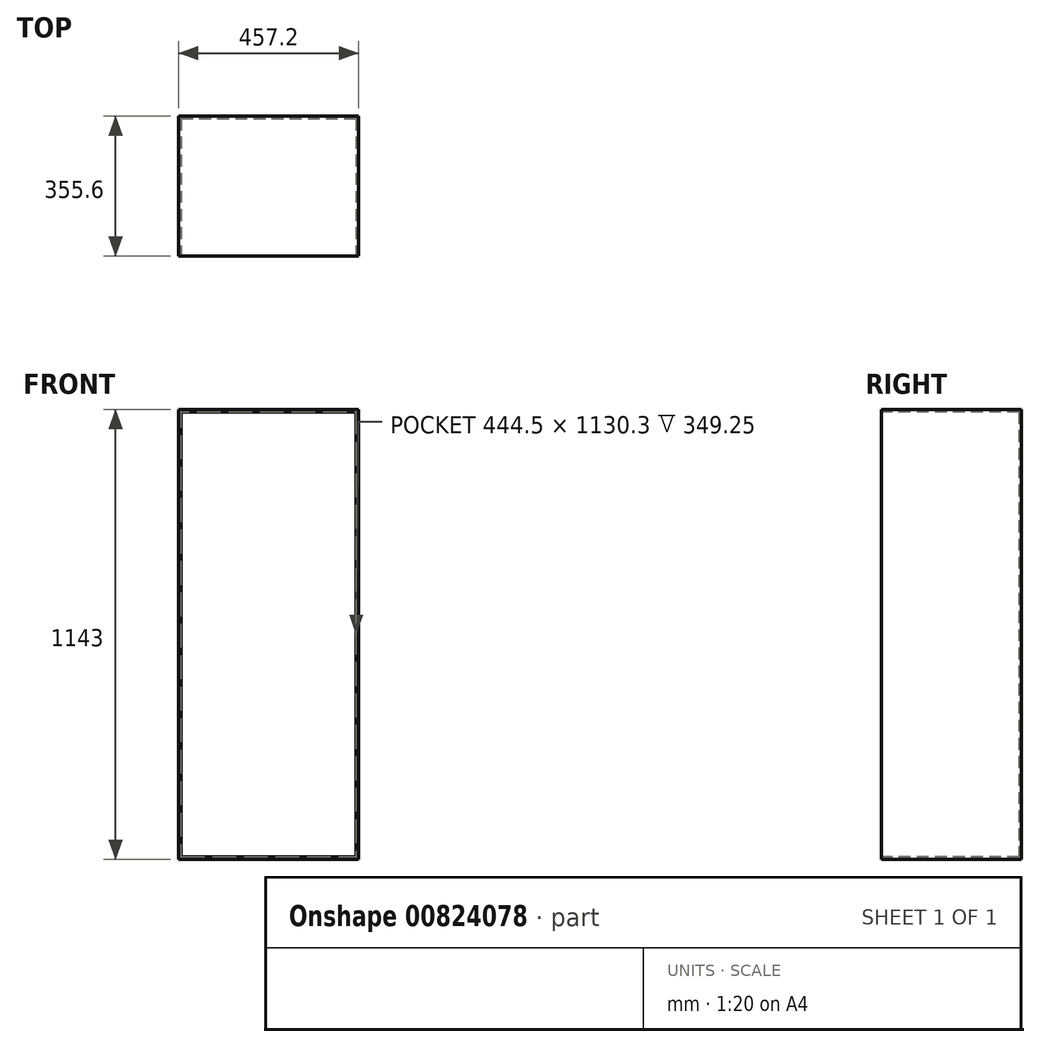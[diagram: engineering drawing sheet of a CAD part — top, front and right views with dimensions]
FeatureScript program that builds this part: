
annotation { "Feature Type Name" : "Feature", "Feature Type Description" : "" }
export const myFeature = defineFeature(function(context is Context, id is Id, definition is map)
    precondition{}
    {
        {
            var Q0;
            Q0=qCreatedBy(makeId("Top.planeOp"),FACE);
            var sketch = newSketch(context, id + "F0", { "sketchPlane" : qUnion([Q0])});
            skLineSegment(sketch, "E0.bottom", {"start": v(228.6, 177.8) * mm, "end": v(-228.6, 177.8) * mm});
            skLineSegment(sketch, "E0.top", {"start": v(228.6, -177.8) * mm, "end": v(-228.6, -177.8) * mm});
            skLineSegment(sketch, "E0.left", {"start": v(228.6, 177.8) * mm, "end": v(228.6, -177.8) * mm});
            skLineSegment(sketch, "E0.right", {"start": v(-228.6, 177.8) * mm, "end": v(-228.6, -177.8) * mm});
            skPoint(sketch, "E0.middle", {"position": v(0, 0) * mm});
            skSolve(sketch);
        }
        {
            var Q0;
            Q0 = qSketchRegion(id + "F0", true);
            extrude(context, id + "F1", {"entities" : qUnion([Q0]), "depth" : 1143 * mm, "offsetDistance" : 25.4 * mm});
        }
        {
            var Q0;
            Q0=makeQuery(id+"F1.opExtrude","SWEPT_FACE",FACE,{"disambiguationData":[OSD([sQuery(id+"F0.wireOp",EDGE,"E0.top")])]});
            var sketch = newSketch(context, id + "F2", { "sketchPlane" : qUnion([Q0])});
            skLineSegment(sketch, "E1.bottom", {"start": v(-222.25, 1136.65) * mm, "end": v(222.25, 1136.65) * mm});
            skLineSegment(sketch, "E1.top", {"start": v(-222.25, 6.35) * mm, "end": v(222.25, 6.35) * mm});
            skLineSegment(sketch, "E1.left", {"start": v(-222.25, 1136.65) * mm, "end": v(-222.25, 6.35) * mm});
            skLineSegment(sketch, "E1.right", {"start": v(222.25, 1136.65) * mm, "end": v(222.25, 6.35) * mm});
            skSolve(sketch);
        }
        {
            var Q0;
            Q0=makeQuery(id+"F2.imprint","IMPRINT",FACE,{"disambiguationData":[TD([[makeQuery(id+"F2.imprint","IMPRINT",EDGE,{"derivedFrom":sQuery(id+"F2.wireOp",EDGE,"E1.bottom")}),-1.0]])]});
            extrude(context, id + "F3", {"entities" : qUnion([Q0]), "operationType" : NewBodyOperationType.REMOVE, "oppositeDirection" : true, "depth" : 349.25 * mm, "offsetDistance" : 25.4 * mm});
        }
    });
